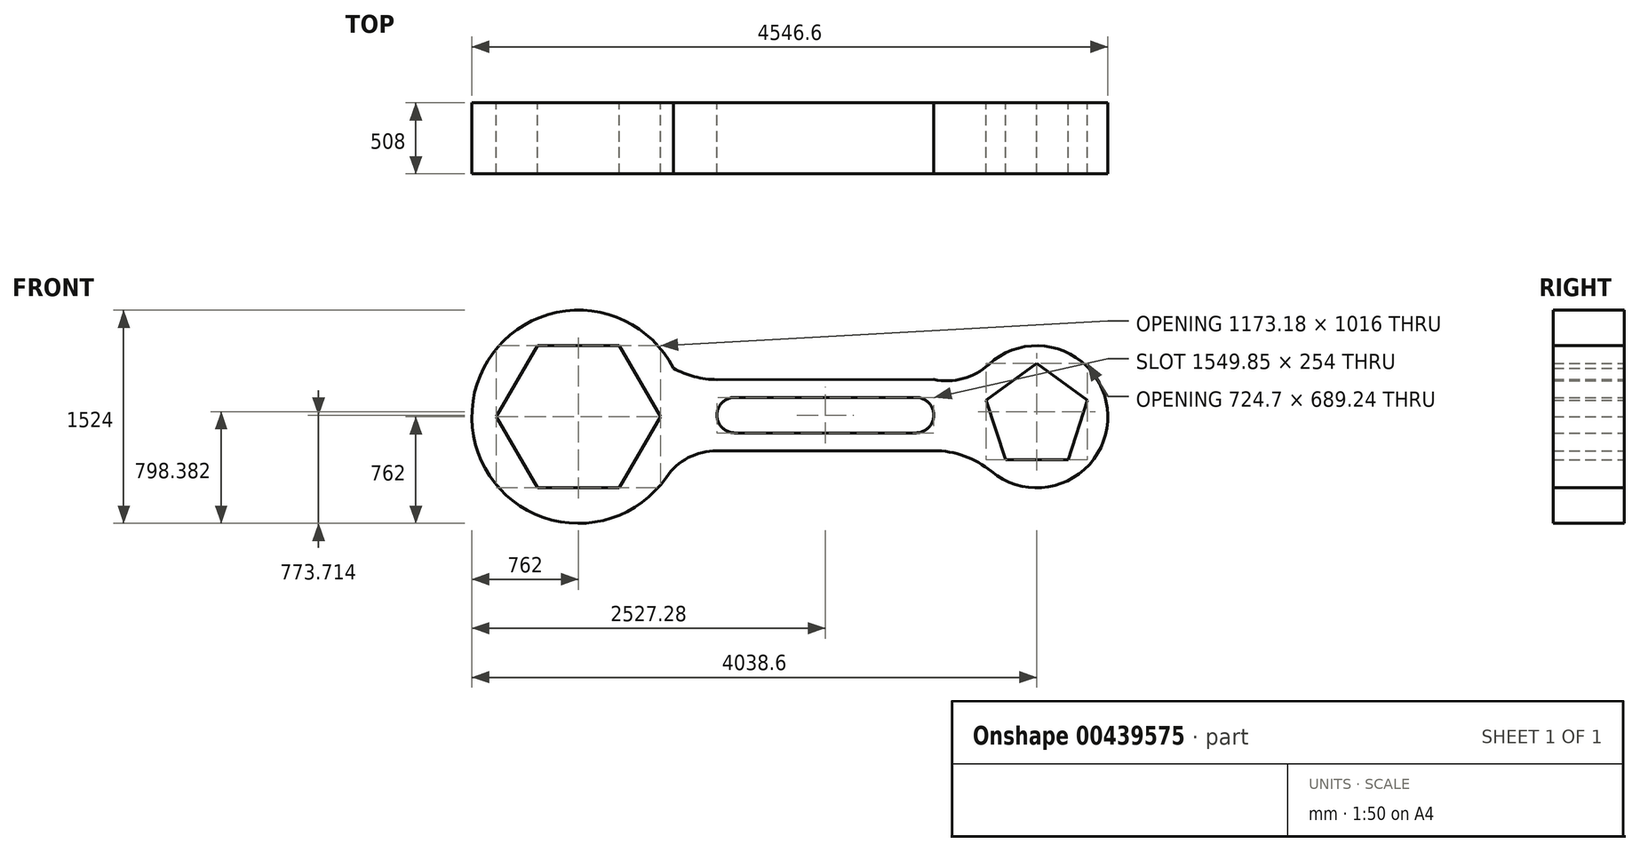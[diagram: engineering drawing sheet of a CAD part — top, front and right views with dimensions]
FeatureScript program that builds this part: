
annotation { "Feature Type Name" : "Feature", "Feature Type Description" : "" }
export const myFeature = defineFeature(function(context is Context, id is Id, definition is map)
    precondition{}
    {
        {
            var Q0;
            Q0=qCreatedBy(makeId("Front.planeOp"),FACE);
            var sketch = newSketch(context, id + "F0", { "sketchPlane" : qUnion([Q0])});
            skCircle(sketch, "E0.cCircle", {"center": v(0, 0) * mm, "radius": 508 * mm, "construction": true});
            skLineSegment(sketch, "E0.0", {"start": v(-293.3, 508) * mm, "end": v(293.3, 508) * mm});
            skLineSegment(sketch, "E0.1", {"start": v(293.3, 508) * mm, "end": v(586.59, 0) * mm});
            skLineSegment(sketch, "E0.2", {"start": v(586.59, 0) * mm, "end": v(293.3, -508) * mm});
            skLineSegment(sketch, "E0.3", {"start": v(293.3, -508) * mm, "end": v(-293.3, -508) * mm});
            skLineSegment(sketch, "E0.4", {"start": v(-293.3, -508) * mm, "end": v(-586.59, 0) * mm});
            skLineSegment(sketch, "E0.5", {"start": v(-586.59, 0) * mm, "end": v(-293.3, 508) * mm});
            skPoint(sketch, "E0.0.midPoint", {"position": v(0, 508) * mm});
            skCircle(sketch, "E1.cCircle", {"center": v(3276.6, 0) * mm, "radius": 308.24 * mm, "construction": true});
            skLineSegment(sketch, "E1.0", {"start": v(3500.55, -308.24) * mm, "end": v(3052.65, -308.24) * mm});
            skLineSegment(sketch, "E1.1", {"start": v(3052.65, -308.24) * mm, "end": v(2914.25, 117.74) * mm});
            skLineSegment(sketch, "E1.2", {"start": v(2914.25, 117.74) * mm, "end": v(3276.6, 381) * mm});
            skLineSegment(sketch, "E1.3", {"start": v(3276.6, 381) * mm, "end": v(3638.95, 117.74) * mm});
            skLineSegment(sketch, "E1.4", {"start": v(3638.95, 117.74) * mm, "end": v(3500.55, -308.24) * mm});
            skPoint(sketch, "E1.0.midPoint", {"position": v(3276.6, -308.24) * mm});
            skCircle(sketch, "E2", {"center": v(0, 0) * mm, "radius": 762 * mm});
            skCircle(sketch, "E3", {"center": v(3276.6, 0) * mm, "radius": 508 * mm});
            skLineSegment(sketch, "E4.trimOffspring", {"start": v(2952.5, 0) * mm, "end": v(2968.36, 0) * mm});
            skArc(sketch, "E5", {"start": v(1117.58, 138.71) * mm, "mid": v(990.35, 11.72) * mm, "end": v(1117.57, -115.29) * mm});
            skArc(sketch, "E6", {"start": v(2412.98, -115.29) * mm, "mid": v(2540.2, 11.71) * mm, "end": v(2412.98, 138.71) * mm});
            skLineSegment(sketch, "E7", {"start": v(1117.58, 138.71) * mm, "end": v(2412.98, 138.71) * mm});
            skLineSegment(sketch, "E8", {"start": v(1117.57, -115.29) * mm, "end": v(2412.98, -115.29) * mm});
            skLineSegment(sketch, "E9.trimOffspring", {"start": v(2540.2, 12.53) * mm, "end": v(2768.8, 14) * mm});
            skLineSegment(sketch, "E10", {"start": v(990.35, 11.71) * mm, "end": v(990.35, 265.71) * mm});
            skLineSegment(sketch, "E11", {"start": v(990.35, 11.71) * mm, "end": v(990.35, -242.29) * mm});
            skLineSegment(sketch, "E12", {"start": v(2540.2, 12.53) * mm, "end": v(2540.2, 266.53) * mm});
            skLineSegment(sketch, "E13", {"start": v(990.35, 265.71) * mm, "end": v(2540.2, 266.53) * mm});
            skLineSegment(sketch, "E14", {"start": v(990.35, -242.29) * mm, "end": v(2540.2, -242.29) * mm});
            skArc(sketch, "E15", {"start": v(678, 347.78) * mm, "mid": v(828.87, 286.53) * mm, "end": v(990.35, 265.71) * mm});
            skArc(sketch, "E16", {"start": v(990.35, -242.29) * mm, "mid": v(785.22, -292.84) * mm, "end": v(627.07, -432.93) * mm});
            skArc(sketch, "E17", {"start": v(2540.2, 266.53) * mm, "mid": v(2749.22, 272.11) * mm, "end": v(2932.15, 373.4) * mm});
            skArc(sketch, "E18", {"start": v(2952.23, -390.96) * mm, "mid": v(2759.22, -280.6) * mm, "end": v(2540.2, -242.29) * mm});
            skPoint(sketch, "E19.start.orphan", {"position": v(762, -1.54) * mm});
            skSolve(sketch);
        }
        {
            var Q0;
            Q0=makeQuery(id+"F0.imprint","IMPRINT",FACE,{"disambiguationData":[TD([[makeQuery(id+"F0.imprint","IMPRINT",EDGE,{"derivedFrom":sQuery(id+"F0.wireOp",EDGE,"E0.0")}),1.0]])]});
            var Q1;
            {var subQ0=sQuery(id+"F0.wireOp",EDGE,"E8");Q1=makeQuery(id+"F0.imprint","IMPRINT",FACE,{"disambiguationData":[TD([[makeQuery(id+"F0.imprint","IMPRINT",EDGE,{"derivedFrom":subQ0}),-1.0]])]});}
            var Q2;
            {var subQ1=sQuery(id+"F0.wireOp",EDGE,"E7");Q2=makeQuery(id+"F0.imprint","IMPRINT",FACE,{"disambiguationData":[TD([[makeQuery(id+"F0.imprint","IMPRINT",EDGE,{"derivedFrom":subQ1}),1.0]])]});}
            var Q3;
            Q3=makeQuery(id+"F0.imprint","IMPRINT",FACE,{"disambiguationData":[TD([[makeQuery(id+"F0.imprint","IMPRINT",EDGE,{"derivedFrom":sQuery(id+"F0.wireOp",EDGE,"E10")}),1.0]])]});
            var Q4;
            {var subQ0=sQuery(id+"F0.wireOp",EDGE,"E9.trimOffspring");Q4=makeQuery(id+"F0.imprint","IMPRINT",FACE,{"disambiguationData":[TD([[makeQuery(id+"F0.imprint","IMPRINT",EDGE,{"derivedFrom":subQ0}),1.0]])]});}
            var Q5;
            {var subQ3=sQuery(id+"F0.wireOp",EDGE,"E1.0");Q5=makeQuery(id+"F0.imprint","IMPRINT",FACE,{"disambiguationData":[TD([[makeQuery(id+"F0.imprint","IMPRINT",EDGE,{"derivedFrom":subQ3}),1.0]])]});}
            extrude(context, id + "F1", {"entities" : qUnion([Q0, Q1, Q2, Q3, Q4, Q5]), "depth" : 508 * mm});
        }
    });
